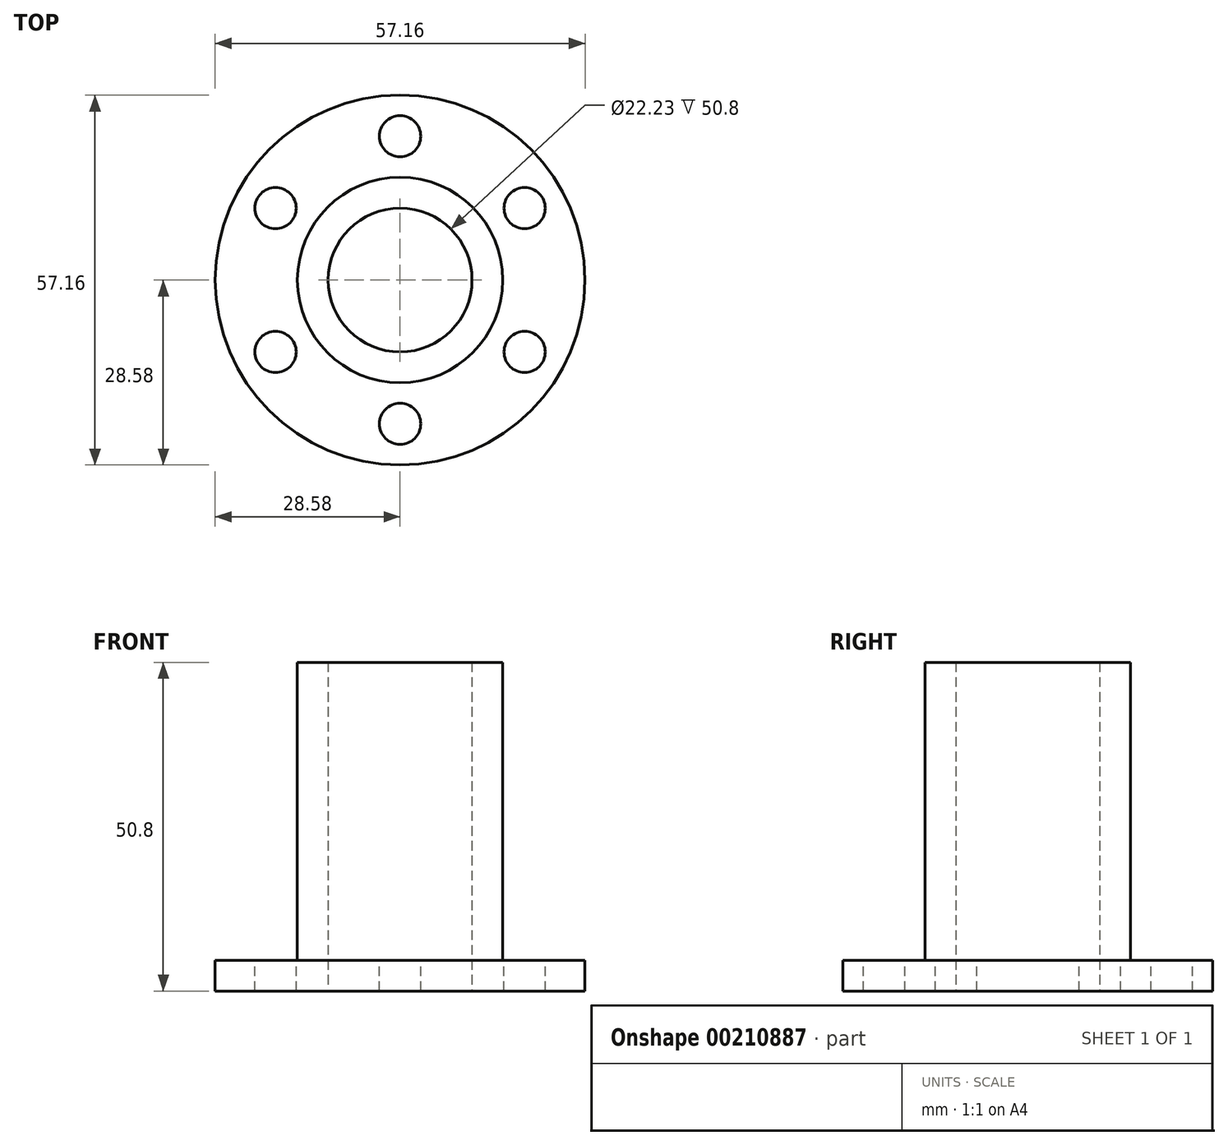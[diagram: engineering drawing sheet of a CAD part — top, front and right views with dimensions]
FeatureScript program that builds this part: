
annotation { "Feature Type Name" : "Feature", "Feature Type Description" : "" }
export const myFeature = defineFeature(function(context is Context, id is Id, definition is map)
    precondition{}
    {
        {
            var Q0;
            Q0=qCreatedBy(makeId("Front.planeOp"),FACE);
            var sketch = newSketch(context, id + "F0", { "sketchPlane" : qUnion([Q0])});
            skLineSegment(sketch, "E0", {"start": v(11.11, 0) * mm, "end": v(11.11, 50.8) * mm});
            skLineSegment(sketch, "E1", {"start": v(11.11, 50.8) * mm, "end": v(15.87, 50.8) * mm});
            skLineSegment(sketch, "E2", {"start": v(15.87, 50.8) * mm, "end": v(15.88, 4.76) * mm});
            skLineSegment(sketch, "E3", {"start": v(15.88, 4.76) * mm, "end": v(28.58, 4.76) * mm});
            skLineSegment(sketch, "E4", {"start": v(28.58, 4.76) * mm, "end": v(28.58, 0) * mm});
            skLineSegment(sketch, "E5", {"start": v(28.58, 0) * mm, "end": v(11.11, 0) * mm});
            skLineSegment(sketch, "E6", {"start": v(0, 0) * mm, "end": v(0, 49.94) * mm, "construction": true});
            skSolve(sketch);
        }
        {
            var Q0;
            Q0=makeQuery(id+"F0.imprint","IMPRINT",FACE,{"disambiguationData":[TD([[makeQuery(id+"F0.imprint","IMPRINT",EDGE,{"derivedFrom":sQuery(id+"F0.wireOp",EDGE,"E0")}),-1.0]])]});
            var Q1;
            Q1=sQuery(id+"F0.wireOp",EDGE,"E6");
            revolve(context, id + "F1", {"entities" : qUnion([Q0]), "axis" : qUnion([Q1]), "revolveType" : RevolveType.FULL});
        }
        {
            var Q0;
            Q0=makeQuery(id+"F1.opRevolve","SWEPT_FACE",FACE,{"disambiguationData":[OSD([sQuery(id+"F0.wireOp",EDGE,"E3")])]});
            var sketch = newSketch(context, id + "F2", { "sketchPlane" : qUnion([Q0])});
            skCircle(sketch, "E7", {"center": v(0, 0) * mm, "radius": 22.23 * mm, "construction": true});
            skCircle(sketch, "E8", {"center": v(0, 22.23) * mm, "radius": 3.19 * mm});
            skCircle(sketch, "E9.1.0", {"center": v(19.25, 11.11) * mm, "radius": 3.19 * mm});
            skCircle(sketch, "E9.2.0", {"center": v(19.25, -11.11) * mm, "radius": 3.19 * mm});
            skCircle(sketch, "E9.3.0", {"center": v(0, -22.23) * mm, "radius": 3.19 * mm});
            skCircle(sketch, "E9.4.0", {"center": v(-19.25, -11.11) * mm, "radius": 3.19 * mm});
            skCircle(sketch, "E9.5.0", {"center": v(-19.25, 11.11) * mm, "radius": 3.19 * mm});
            skLineSegment(sketch, "E9.anchor1", {"start": v(0, 0) * mm, "end": v(0, 22.23) * mm, "construction": true});
            skLineSegment(sketch, "E9.anchor2", {"start": v(0, 0) * mm, "end": v(-19.25, 11.11) * mm, "construction": true});
            skSolve(sketch);
        }
        {
            var Q0;
            Q0 = qSketchRegion(id + "F2", true);
            extrude(context, id + "F3", {"entities" : qUnion([Q0]), "operationType" : NewBodyOperationType.REMOVE, "oppositeDirection" : true, "depth" : 25.4 * mm});
        }
    });
